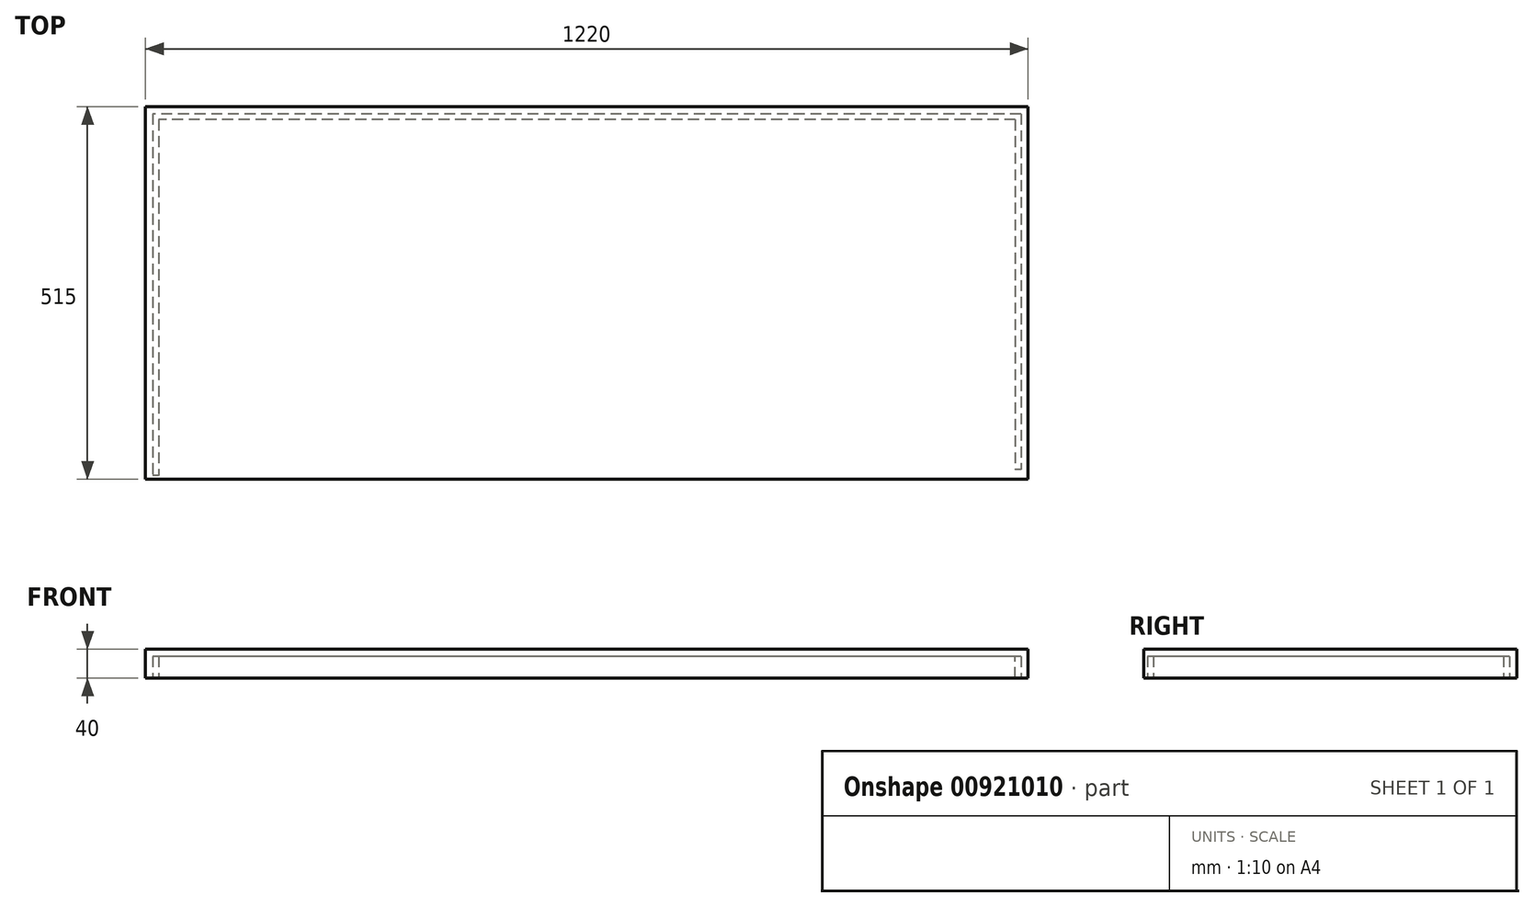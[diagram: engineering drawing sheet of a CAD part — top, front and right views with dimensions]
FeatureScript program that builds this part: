
annotation { "Feature Type Name" : "Feature", "Feature Type Description" : "" }
export const myFeature = defineFeature(function(context is Context, id is Id, definition is map)
    precondition{}
    {
        {
            var Q0;
            Q0=qCreatedBy(makeId("Top.planeOp"),FACE);
            var sketch = newSketch(context, id + "F0", { "sketchPlane" : qUnion([Q0])});
            skLineSegment(sketch, "E0.bottom", {"start": v(-610, 257.5) * mm, "end": v(610, 257.5) * mm});
            skLineSegment(sketch, "E0.top", {"start": v(-610, -257.5) * mm, "end": v(610, -257.5) * mm});
            skLineSegment(sketch, "E0.left", {"start": v(-610, 257.5) * mm, "end": v(-610, -257.5) * mm});
            skLineSegment(sketch, "E0.right", {"start": v(610, 257.5) * mm, "end": v(610, -257.5) * mm});
            skPoint(sketch, "E0.middle", {"position": v(0, 0) * mm});
            skSolve(sketch);
        }
        {
            var Q0;
            Q0=makeQuery(id+"F0.imprint","IMPRINT",FACE,{"disambiguationData":[TD([[makeQuery(id+"F0.imprint","IMPRINT",EDGE,{"derivedFrom":sQuery(id+"F0.wireOp",EDGE,"E0.bottom")}),-1.0]])]});
            extrude(context, id + "F1", {"entities" : qUnion([Q0]), "endBound" : BoundingType.SYMMETRIC, "depth" : 40 * mm, "offsetDistance" : 25 * mm});
        }
        {
            var Q0;
            Q0=makeQuery(id+"F1.opExtrude","CAP_FACE",FACE,{"disambiguationData":[OSD([sQuery(id+"F0.wireOp",EDGE,"E0.bottom"),sQuery(id+"F0.wireOp",EDGE,"E0.top"),sQuery(id+"F0.wireOp",EDGE,"E0.left"),sQuery(id+"F0.wireOp",EDGE,"E0.right")])],"isStart":false});
            var sketch = newSketch(context, id + "F2", { "sketchPlane" : qUnion([Q0])});
            skLineSegment(sketch, "E1.bottom", {"start": v(-600, 247.5) * mm, "end": v(600, 247.5) * mm});
            skLineSegment(sketch, "E1.top", {"start": v(-600, 239.5) * mm, "end": v(600, 239.5) * mm});
            skLineSegment(sketch, "E1.left", {"start": v(-600, 247.5) * mm, "end": v(-600, 239.5) * mm});
            skLineSegment(sketch, "E1.right", {"start": v(600, 247.5) * mm, "end": v(600, 239.5) * mm});
            skSolve(sketch);
        }
        {
            var Q0;
            Q0=qSketchRegion(id+"F2",true);
            extrude(context, id + "F3", {"entities" : qUnion([Q0]), "operationType" : NewBodyOperationType.REMOVE, "oppositeDirection" : true, "depth" : 30 * mm, "offsetDistance" : 25 * mm});
        }
        {
            var Q0;
            Q0=makeQuery(id+"F1.opExtrude","CAP_FACE",FACE,{"disambiguationData":[OSD([sQuery(id+"F0.wireOp",EDGE,"E0.bottom"),sQuery(id+"F0.wireOp",EDGE,"E0.top"),sQuery(id+"F0.wireOp",EDGE,"E0.left"),sQuery(id+"F0.wireOp",EDGE,"E0.right")])],"isStart":false});
            var sketch = newSketch(context, id + "F4", { "sketchPlane" : qUnion([Q0])});
            skLineSegment(sketch, "E2.bottom", {"start": v(-600, 247.5) * mm, "end": v(-592, 247.5) * mm});
            skLineSegment(sketch, "E2.top", {"start": v(-600, -244.5) * mm, "end": v(-592, -244.5) * mm});
            skLineSegment(sketch, "E2.left", {"start": v(-600, 247.5) * mm, "end": v(-600, -244.5) * mm});
            skLineSegment(sketch, "E2.right", {"start": v(-592, 247.5) * mm, "end": v(-592, -244.5) * mm});
            skSolve(sketch);
        }
        {
            var Q0;
            Q0=qSketchRegion(id+"F4",true);
            extrude(context, id + "F5", {"entities" : qUnion([Q0]), "operationType" : NewBodyOperationType.REMOVE, "oppositeDirection" : true, "depth" : 30 * mm, "offsetDistance" : 25 * mm});
        }
        {
            var Q0;
            Q0=makeQuery(id+"F1.opExtrude","CAP_FACE",FACE,{"disambiguationData":[OSD([sQuery(id+"F0.wireOp",EDGE,"E0.bottom"),sQuery(id+"F0.wireOp",EDGE,"E0.top"),sQuery(id+"F0.wireOp",EDGE,"E0.left"),sQuery(id+"F0.wireOp",EDGE,"E0.right")])],"isStart":false});
            var sketch = newSketch(context, id + "F6", { "sketchPlane" : qUnion([Q0])});
            skLineSegment(sketch, "E3.bottom", {"start": v(592, 239.5) * mm, "end": v(600, 239.5) * mm});
            skLineSegment(sketch, "E3.top", {"start": v(592, -252.5) * mm, "end": v(600, -252.5) * mm});
            skLineSegment(sketch, "E3.left", {"start": v(592, 239.5) * mm, "end": v(592, -252.5) * mm});
            skLineSegment(sketch, "E3.right", {"start": v(600, 239.5) * mm, "end": v(600, -252.5) * mm});
            skSolve(sketch);
        }
        {
            var Q0;
            Q0=makeQuery(id+"F6.imprint","IMPRINT",FACE,{"disambiguationData":[TD([[makeQuery(id+"F6.imprint","IMPRINT",EDGE,{"derivedFrom":sQuery(id+"F6.wireOp",EDGE,"E3.bottom")}),-1.0]])]});
            extrude(context, id + "F7", {"entities" : qUnion([Q0]), "operationType" : NewBodyOperationType.REMOVE, "oppositeDirection" : true, "depth" : 30 * mm, "offsetDistance" : 25 * mm});
        }
        {
            var Q0;
            Q0=makeQuery(id+"F1.opExtrude","SWEPT_BODY",BODY,{"disambiguationData":[OSD([sQuery(id+"F0.wireOp",EDGE,"E0.bottom"),sQuery(id+"F0.wireOp",EDGE,"E0.top"),sQuery(id+"F0.wireOp",EDGE,"E0.left"),sQuery(id+"F0.wireOp",EDGE,"E0.right")])]});
            var Q1;
            Q1=makeQuery(id+"F1.opExtrude","CAP_EDGE",EDGE,{"disambiguationData":[OSD([sQuery(id+"F0.wireOp",EDGE,"E0.left")])],"isStart":false});
            transform(context, id + "F8", {"entities" : qUnion([Q0]), "transformType" : TransformType.ROTATION, "transformAxis" : qUnion([Q1]), "angle" : 180 * degree, "makeCopy" : false});
        }
    });
